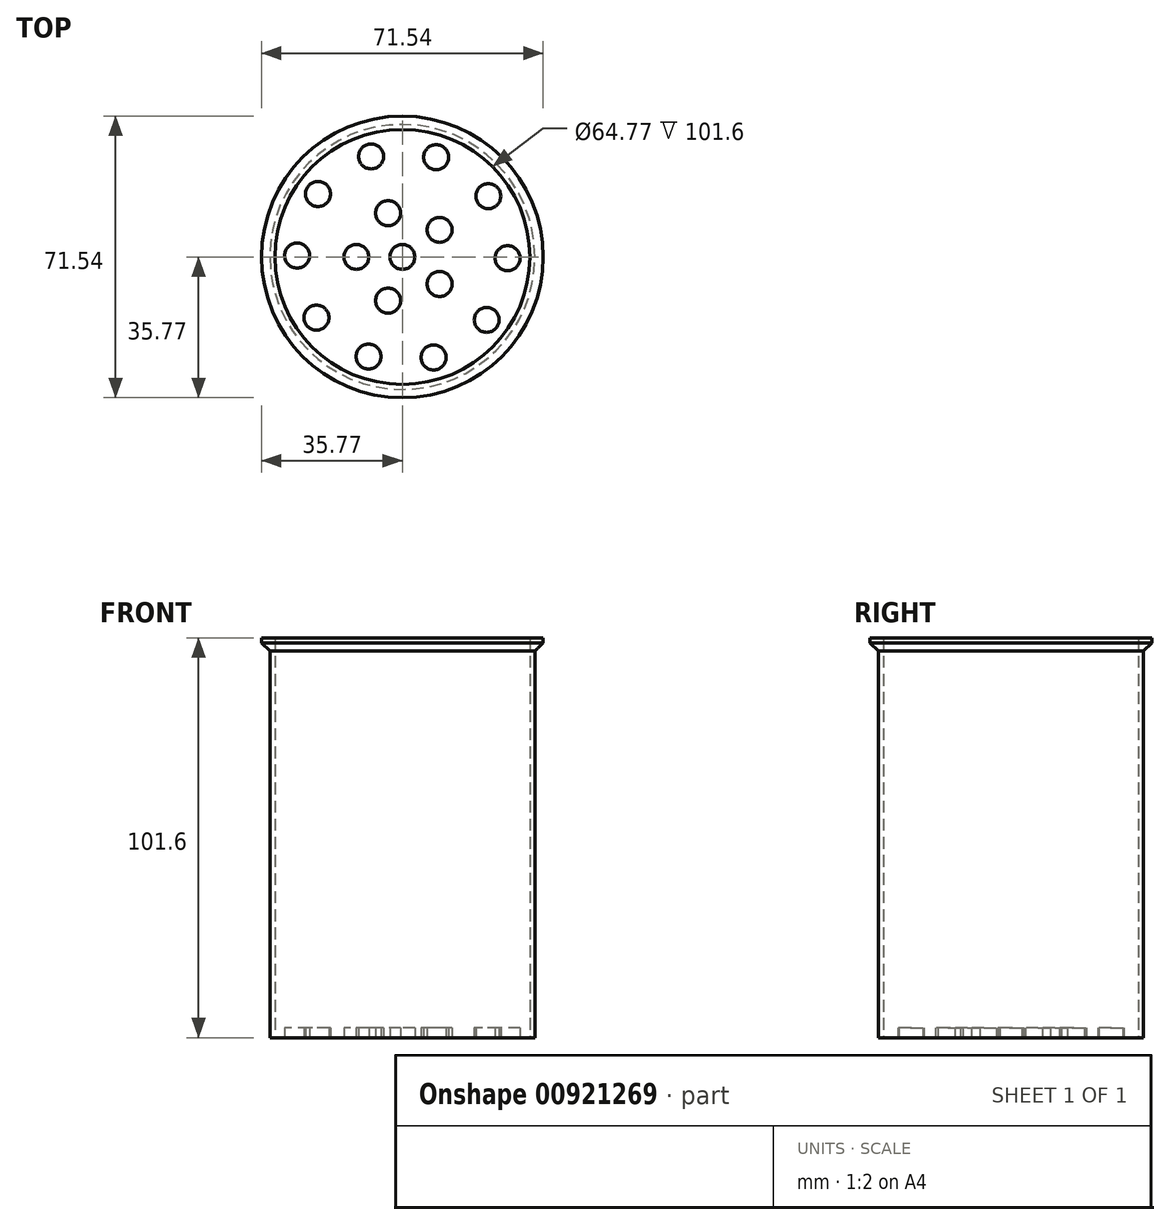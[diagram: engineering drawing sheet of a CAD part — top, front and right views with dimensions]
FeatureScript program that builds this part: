
annotation { "Feature Type Name" : "Feature", "Feature Type Description" : "" }
export const myFeature = defineFeature(function(context is Context, id is Id, definition is map)
    precondition{}
    {
        {
            var Q0;
            Q0=qCreatedBy(makeId("Top.planeOp"),FACE);
            var sketch = newSketch(context, id + "F0", { "sketchPlane" : qUnion([Q0])});
            skCircle(sketch, "E0", {"center": v(0, 0) * mm, "radius": 33.66 * mm});
            skCircle(sketch, "E1", {"center": v(0, 0) * mm, "radius": 32.39 * mm});
            skSolve(sketch);
        }
        {
            var Q0;
            Q0=makeQuery(id+"F0.imprint","IMPRINT",FACE,{"disambiguationData":[TD([[makeQuery(id+"F0.imprint","IMPRINT",EDGE,{"derivedFrom":sQuery(id+"F0.wireOp",EDGE,"E0")}),1.0]])]});
            var Q1;
            Q1=sQuery(id+"F0.wireOp",EDGE,"E0");
            extrude(context, id + "F1", {"entities" : qUnion([Q0]), "surfaceEntities" : qUnion([Q1]), "depth" : 101.6 * mm, "offsetDistance" : 25.4 * mm});
        }
        {
            var Q0;
            Q0=qCreatedBy(makeId("Top.planeOp"),FACE);
            var sketch = newSketch(context, id + "F2", { "sketchPlane" : qUnion([Q0])});
            skCircle(sketch, "E2", {"center": v(0, 0) * mm, "radius": 33.3 * mm});
            skSolve(sketch);
        }
        {
            var Q0;
            Q0 = qSketchRegion(id + "F2", true);
            extrude(context, id + "F3", {"entities" : qUnion([Q0]), "operationType" : NewBodyOperationType.ADD, "depth" : 2.54 * mm, "offsetDistance" : 25.4 * mm});
        }
        {
            var Q0;
            Q0=makeQuery(id+"F3.boolean.opBoolean","MERGE",FACE,{"derivedFrom":[makeQuery(id+"F1.opExtrude","CAP_FACE",FACE,{"disambiguationData":[OSD([sQuery(id+"F0.wireOp",EDGE,"E0"),sQuery(id+"F0.wireOp",EDGE,"E1")])],"isStart":true}),makeQuery(id+"F3.opExtrude","CAP_FACE",FACE,{"disambiguationData":[OSD([sQuery(id+"F2.wireOp",EDGE,"E2")])],"isStart":true})]});
            var sketch = newSketch(context, id + "F4", { "sketchPlane" : qUnion([Q0])});
            skCircle(sketch, "E3", {"center": v(0, 0) * mm, "radius": 3.18 * mm});
            skCircle(sketch, "E4", {"center": v(-11.7, 0) * mm, "radius": 3.18 * mm});
            skCircle(sketch, "E5.1.0", {"center": v(-3.61, -11.12) * mm, "radius": 3.18 * mm});
            skCircle(sketch, "E5.2.0", {"center": v(9.46, -6.87) * mm, "radius": 3.18 * mm});
            skCircle(sketch, "E5.3.0", {"center": v(9.46, 6.87) * mm, "radius": 3.18 * mm});
            skCircle(sketch, "E5.4.0", {"center": v(-3.61, 11.12) * mm, "radius": 3.18 * mm});
            skCircle(sketch, "E6", {"center": v(-26.74, -0.34) * mm, "radius": 3.18 * mm});
            skCircle(sketch, "E7.1.0", {"center": v(-21.43, -16) * mm, "radius": 3.18 * mm});
            skCircle(sketch, "E7.2.0", {"center": v(-7.94, -25.54) * mm, "radius": 3.18 * mm});
            skCircle(sketch, "E7.3.0", {"center": v(8.59, -25.32) * mm, "radius": 3.18 * mm});
            skCircle(sketch, "E7.4.0", {"center": v(21.83, -15.44) * mm, "radius": 3.18 * mm});
            skCircle(sketch, "E7.5.0", {"center": v(26.74, 0.34) * mm, "radius": 3.18 * mm});
            skCircle(sketch, "E7.6.0", {"center": v(21.43, 16) * mm, "radius": 3.18 * mm});
            skCircle(sketch, "E7.7.0", {"center": v(7.94, 25.54) * mm, "radius": 3.18 * mm});
            skCircle(sketch, "E7.8.0", {"center": v(-8.59, 25.32) * mm, "radius": 3.18 * mm});
            skCircle(sketch, "E7.9.0", {"center": v(-21.83, 15.44) * mm, "radius": 3.18 * mm});
            skCircle(sketch, "E8.0.0", {"center": v(0, 0) * mm, "radius": 32.39 * mm});
            skSolve(sketch);
        }
        {
            var Q0;
            Q0 = qSketchRegion(id + "F4", true);
            extrude(context, id + "F5", {"entities" : qUnion([Q0]), "operationType" : NewBodyOperationType.REMOVE, "oppositeDirection" : true, "depth" : 25.4 * mm, "offsetDistance" : 25.4 * mm});
        }
        {
            var Q0;
            Q0=makeQuery(id+"F1.opExtrude","CAP_FACE",FACE,{"disambiguationData":[OSD([sQuery(id+"F0.wireOp",EDGE,"E0"),sQuery(id+"F0.wireOp",EDGE,"E1")])],"isStart":false});
            var sketch = newSketch(context, id + "F6", { "sketchPlane" : qUnion([Q0])});
            skCircle(sketch, "E9", {"center": v(0, 0) * mm, "radius": 35.77 * mm});
            skCircle(sketch, "E10", {"center": v(0, 0) * mm, "radius": 33.02 * mm});
            skSolve(sketch);
        }
        {
            var Q0;
            Q0 = qSketchRegion(id + "F6", true);
            extrude(context, id + "F7", {"entities" : qUnion([Q0]), "operationType" : NewBodyOperationType.ADD, "depth" : -6.35 * mm, "offsetDistance" : 25.4 * mm});
        }
        {
            var Q0;
            Q0=makeQuery(id+"F7.opExtrude","CAP_EDGE",EDGE,{"disambiguationData":[OSD([sQuery(id+"F6.wireOp",EDGE,"E9")])],"isStart":false});
            chamfer(context, id + "F8", {"entities" : qUnion([Q0]), "width" : 5.08 * mm, "tangentPropagation" : true});
        }
    });
